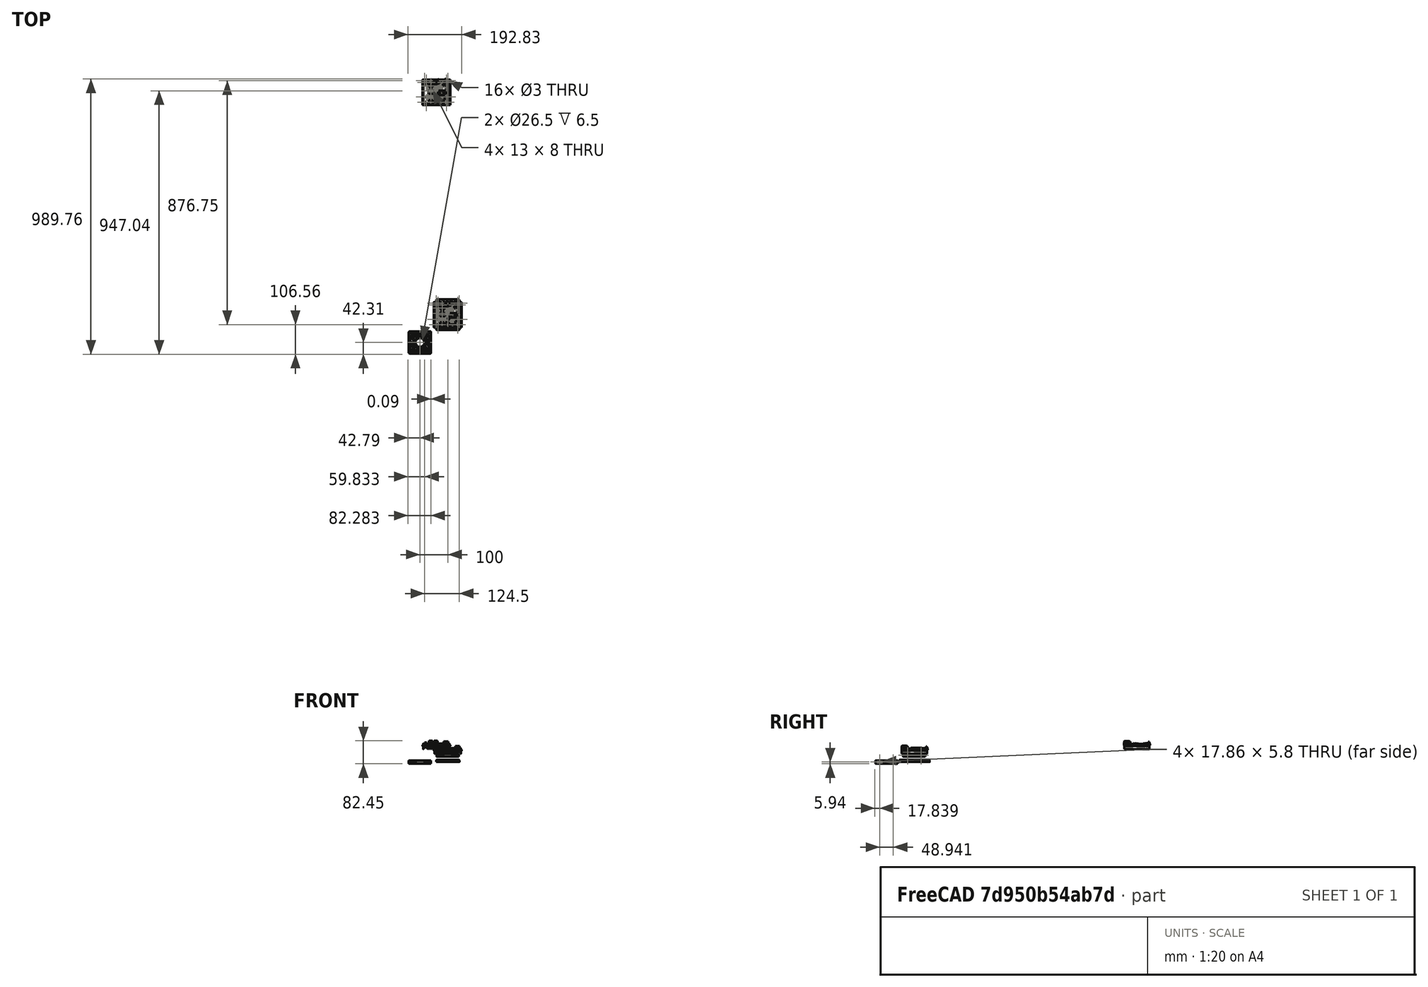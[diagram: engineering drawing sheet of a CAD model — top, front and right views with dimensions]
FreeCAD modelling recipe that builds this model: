
FCSTD DOCUMENT  (FreeCAD 1.0R39109 (Git))
Label: n2Holder
License: All rights reserved
LicenseURL: http://en.wikipedia.org/wiki/All_rights_reserved
objects: Part::Feature×20, App::Part×3, Sketcher::SketchObject×2, Part::Extrusion×2, Part::Fillet×2, Part::Cut×1, Part::Compound×1
note: 30 computed .brp shape members not serialized (recipe doc carries the construction recipe); baked Part::Feature solids carry a one-line shape summary decoded from their .brp

FEATURE [Part::Feature] Part__Feature318  label="Heat Sink002"
  shape: bbox 100 x 91 x 19 mm, 161 faces (baked)
FEATURE [Part::Feature] Part__Feature319  label="Component011"
  Placement = pos=(-40,-40,21) rot=(0,1,0;3.14159rad)
  shape: bbox 83.92 x 84.69 x 8.441 mm, 27 faces (baked)
FEATURE [Part::Feature] Part__Feature320  label="80mmFanSlim003"
  shape: bbox 82.8 x 82.8 x 10.8 mm, 179 faces (baked)
FEATURE [App::Part] Part008  label="80mm_Fan002"
  Group = -> [Part__Feature319,Part__Feature320]
  Origin = -> Origin033
  Placement = pos=(0,0,0) rot=(1,0,0;3.14159rad)
FEATURE [Part::Feature] Part__Feature321  label="Battery Holder002"
  shape: bbox 28.5 x 16 x 6 mm, 91 faces (baked)
FEATURE [Part::Feature] Part__Feature322  label="DC Jack002"
  shape: bbox 7.6 x 11.5 x 9.75 mm, 10 faces (baked)
FEATURE [Part::Feature] Part__Feature323  label="PCB002"
  shape: bbox 90 x 90 x 3.3 mm, 59 faces (baked)
FEATURE [Part::Feature] Part__Feature324  label="HDMI002"
  shape: bbox 14.51 x 11.61 x 5.506 mm, 31 faces (baked)
FEATURE [Part::Feature] Part__Feature325  label="Ethernet002"
  shape: bbox 15.9 x 21.4 x 13.5 mm, 25 faces (baked)
FEATURE [Part::Feature] Part__Feature326  label="USB 3.0 B002"
  shape: bbox 14.55 x 17.5 x 16.15 mm, 36 faces (baked)
FEATURE [Part::Feature] Part__Feature327  label="USB 3.0 A002"
  shape: bbox 14.55 x 17.5 x 16.15 mm, 36 faces (baked)
FEATURE [Part::Feature] Part__Feature328  label="Audio Jack002"
  shape: bbox 6.5 x 14 x 4 mm, 10 faces (baked)
FEATURE [Part::Feature] Part__Feature329  label="Fan Plug002"
  shape: bbox 3.75 x 7.5 x 4.75 mm, 32 faces (baked)
FEATURE [Part::Feature] Part__Feature330  label="REMOCON002"
  shape: bbox 7.006 x 5.006 x 12.01 mm, 30 faces (baked)
FEATURE [Part::Feature] Part__Feature331  label="eMMC002"
  shape: bbox 13.5 x 18.5 x 2.8 mm, 33 faces (baked)
FEATURE [Part::Feature] Part__Feature332  label="MicroUSB002"
  shape: bbox 7.012 x 4.616 x 3.511 mm, 31 faces (baked)
FEATURE [Part::Feature] Part__Feature333  label="Switch002"
  shape: bbox 9 x 5.74 x 3.5 mm, 11 faces (baked)
FEATURE [Part::Feature] Part__Feature334  label="MicroSD Card Socket002"
  shape: bbox 11.5 x 5.5 x 3.5 mm, 11 faces (baked)
FEATURE [Part::Feature] Part__Feature335  label="7 Pin Header002"
  shape: bbox 17.5 x 2.5 x 8 mm, 41 faces (baked)
FEATURE [Part::Feature] Part__Feature336  label="UART002"
  shape: bbox 5 x 12.5 x 6 mm, 43 faces (baked)
FEATURE [Part::Feature] Part__Feature337  label="40 Pin Header002"
  shape: bbox 5 x 50 x 8 mm, 206 faces (baked)
FEATURE [App::Part] Odroid_N2__v006  label="Odroid-N2+ v006"
  Group = -> [Part__Feature318,Part__Feature321,Part__Feature322,Part__Feature323,Part__Feature324,Part__Feature325,Part__Feature326,Part__Feature327,Part__Feature328,Part__Feature329,Part__Feature330,Part__Feature331,Part__Feature332,Part__Feature333,Part__Feature334,Part__Feature335,Part__Feature336,Part__Feature337]
  Origin = -> Origin034
  Placement = pos=(-59,-819.5,-41.5) rot=(0,0,1;0rad)
FEATURE [App::Part] Part009  label="N2+002"
  Group = -> [Part008,Odroid_N2__v006]
  Origin = -> Origin035
  Placement = pos=(100,20,25) rot=(-1,0,0;0rad)
FEATURE [Sketcher::SketchObject] Sketch012
  ArcFitTolerance = 1e-06
  FullyConstrained = true
  MakeInternals = false
  sketch-geometry (22):
    g0: LineSegment StartX=18 StartY=115 StartZ=0 EndX=18 EndY=5 EndZ=0
    g1: LineSegment StartX=18 StartY=5 StartZ=0 EndX=102 EndY=5 EndZ=0
    g2: LineSegment StartX=102 StartY=5 StartZ=0 EndX=102 EndY=115 EndZ=0
    g3: LineSegment StartX=102 StartY=115 StartZ=0 EndX=18 EndY=115 EndZ=0
    g4: LineSegment StartX=30 StartY=105 StartZ=0 EndX=30 EndY=15 EndZ=0
    g5: LineSegment StartX=30 StartY=15 StartZ=0 EndX=90 EndY=15 EndZ=0
    g6: LineSegment StartX=90 StartY=15 StartZ=0 EndX=90 EndY=105 EndZ=0
    g7: LineSegment StartX=90 StartY=105 StartZ=0 EndX=30 EndY=105 EndZ=0
    g8: Circle CenterX=24.3 CenterY=95.75 CenterZ=0 NormalX=0 NormalY=0 NormalZ=1 AngleXU=0 Radius=1.625
    g9: Circle CenterX=95.8 CenterY=95.75 CenterZ=0 NormalX=0 NormalY=0 NormalZ=1 AngleXU=0 Radius=1.625
    g10: Circle CenterX=95.8 CenterY=24.25 CenterZ=0 NormalX=0 NormalY=0 NormalZ=1 AngleXU=0 Radius=1.625
    g11: Circle CenterX=24.3 CenterY=24.25 CenterZ=0 NormalX=0 NormalY=0 NormalZ=1 AngleXU=0 Radius=1.625
    g12: Circle CenterX=28 CenterY=10 CenterZ=0 NormalX=0 NormalY=0 NormalZ=1 AngleXU=0 Radius=1.625
    g13: Circle CenterX=43 CenterY=10 CenterZ=0 NormalX=0 NormalY=0 NormalZ=1 AngleXU=0 Radius=1.625
    g14: Circle CenterX=58 CenterY=10 CenterZ=0 NormalX=0 NormalY=0 NormalZ=1 AngleXU=0 Radius=1.625
    g15: Circle CenterX=73 CenterY=10 CenterZ=0 NormalX=0 NormalY=0 NormalZ=1 AngleXU=0 Radius=1.625
    g16: Circle CenterX=88 CenterY=10 CenterZ=0 NormalX=0 NormalY=0 NormalZ=1 AngleXU=0 Radius=1.625
    g17: Circle CenterX=28 CenterY=110 CenterZ=0 NormalX=0 NormalY=0 NormalZ=1 AngleXU=0 Radius=1.625
    g18: Circle CenterX=43 CenterY=110 CenterZ=0 NormalX=0 NormalY=0 NormalZ=1 AngleXU=0 Radius=1.625
    g19: Circle CenterX=58 CenterY=110 CenterZ=0 NormalX=0 NormalY=0 NormalZ=1 AngleXU=0 Radius=1.625
    g20: Circle CenterX=73 CenterY=110 CenterZ=0 NormalX=0 NormalY=0 NormalZ=1 AngleXU=0 Radius=1.625
    g21: Circle CenterX=88 CenterY=110 CenterZ=0 NormalX=0 NormalY=0 NormalZ=1 AngleXU=0 Radius=1.625
  constraints (59):
    c: Vertical(g0)
    c: Coincident(g1,g0)
    c: Horizontal(g1)
    c: Vertical(g2)
    c: Coincident(g3,g2)
    c: Coincident(g3,g0)
    c: Horizontal(g3)
    c: Coincident(g4,g5)
    c: Coincident(g5,g6)
    c: Coincident(g6,g7)
    c: Coincident(g7,g4)
    c: Vertical(g4)
    c: Vertical(g6)
    c: Horizontal(g5)
    c: Horizontal(g7)
    c: DistanceY(g0) = 5
    c: DistanceX(g0) = 18
    c: DistanceX(g0,g4) = 12
    c: DistanceX(g5,g5) = 60
    c: Coincident(g1,g2)
    c: DistanceX(g5,g1) = 12
    c: DistanceY(g0,g4) = 10
    c: DistanceY(g4,g4) = 90
    c: DistanceY(g4,g0) = 10
    c: Equal(g12, g13-g16) x4
    c: Equal(g12,g10)
    c: Equal(g12,g9)
    c: Equal(g12,g8)
    c: Equal(g12,g11)
    c: Equal(g12, g17-g21) x5
    c: Diameter(g12) = 3.25
    c: Horizontal(g12,g13)
    c: Horizontal(g13,g14)
    c: Horizontal(g14,g15)
    c: Horizontal(g15,g16)
    c: Horizontal(g17,g18)
    c: Horizontal(g18,g19)
    c: Horizontal(g19,g20)
    c: Horizontal(g20,g21)
    c: Horizontal(g8,g9)
    c: Horizontal(g11,g10)
    c: Vertical(g11,g8)
    c: DistanceX(g12,g13) = 15
    c: DistanceX(g13,g14) = 15
    c: Distance(g14,g15) = 15
    c: Distance(g15,g16) = 15
    c: DistanceX(g0,g12) = 10
    c: DistanceY(g0,g12) = 5
    c: DistanceY(g17,g0) = 5
    c: Vertical(g17,g12)
    c: Vertical(g18,g13)
    c: Vertical(g19,g14)
    c: Vertical(g15,g20)
    c: Vertical(g16,g21)
    c: Vertical(g10,g9)
    c: DistanceX(g11) = 24.3
    c: DistanceY(g11) = 24.25
    c: DistanceX(g11,g10) = 71.5
    c: DistanceY(g11,g8) = 71.5
FEATURE [Part::Extrusion] Extrude012
  Base = -> Sketch012
  Dir = (0,0,1)
  DirMode = 2
  FaceMakerClass = Part::FaceMakerBullseye
  FaceMakerMode = 3
  LengthFwd = 8
  LengthRev = 0
  Solid = true
  Symmetric = false
FEATURE [Part::Fillet] Fillet018
  Base = -> Extrude012
  EdgeLinks = -> Extrude012 [Edge1,Edge2,Edge4,Edge5,Edge7,Edge8,Edge10,Edge12,Edge16,Edge19,Edge22,Edge24]
  Edges = 12 edges r=3: [Edge1,Edge2,Edge4,Edge5,Edge7,Edge8,Edge10,Edge12,Edge16,Edge19,Edge22,Edge24]
FEATURE [Part::Fillet] Fillet019
  Base = -> Fillet018
  EdgeLinks = -> Fillet018 [Edge55,Edge57,Edge59,Edge61,Edge63,Edge65,Edge67,Edge69,Edge71,Edge73,Edge75,Edge77,Edge81]
  Edges = 13 edges r=0.25: [Edge55,Edge57,Edge59,Edge61,Edge63,Edge65,Edge67,Edge69,Edge71,Edge73,Edge75,Edge77,Edge81]
FEATURE [Sketcher::SketchObject] Sketch013
  ArcFitTolerance = 1e-06
  FullyConstrained = true
  MakeInternals = false
  sketch-geometry (4):
    g0: Circle CenterX=24.3 CenterY=95.75 CenterZ=0 NormalX=0 NormalY=0 NormalZ=1 AngleXU=0 Radius=3
    g1: Circle CenterX=95.8 CenterY=95.75 CenterZ=0 NormalX=0 NormalY=0 NormalZ=1 AngleXU=0 Radius=3
    g2: Circle CenterX=95.8 CenterY=24.25 CenterZ=0 NormalX=0 NormalY=0 NormalZ=1 AngleXU=0 Radius=3
    g3: Circle CenterX=24.3 CenterY=24.25 CenterZ=0 NormalX=0 NormalY=0 NormalZ=1 AngleXU=0 Radius=3
  constraints (12):
    c: Horizontal(g0,g1)
    c: Horizontal(g3,g2)
    c: Vertical(g3,g0)
    c: Vertical(g2,g1)
    c: DistanceX(g3) = 24.3
    c: DistanceY(g3) = 24.25
    c: DistanceX(g3,g2) = 71.5
    c: DistanceY(g3,g0) = 71.5
    c: Equal(g3,g2)
    c: Equal(g3,g1)
    c: Equal(g3,g0)
    c: Diameter(g3) = 6
FEATURE [Part::Extrusion] Extrude013
  Base = -> Sketch013
  Dir = (0,0,1)
  DirMode = 2
  FaceMakerClass = Part::FaceMakerBullseye
  FaceMakerMode = 3
  LengthFwd = 3.5
  LengthRev = 0
  Solid = true
  Symmetric = false
FEATURE [Part::Cut] Cut021  label="n2Holder"
  Base = -> Fillet019
  Tool = -> Extrude013
FEATURE [Part::Compound] Compound002  label="n2WithTheHolder"
  Links = -> [Part009,Cut021]
